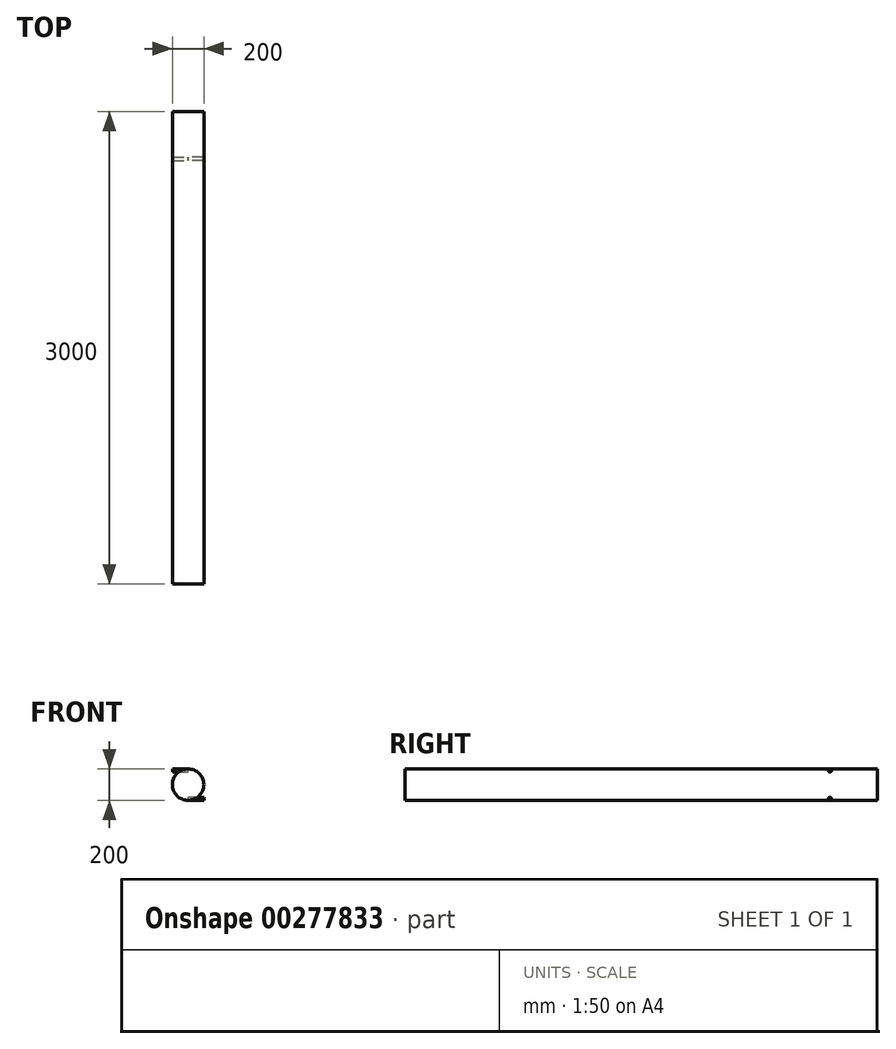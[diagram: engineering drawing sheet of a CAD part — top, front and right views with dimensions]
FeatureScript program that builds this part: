
annotation { "Feature Type Name" : "Feature", "Feature Type Description" : "" }
export const myFeature = defineFeature(function(context is Context, id is Id, definition is map)
    precondition{}
    {
        {
            var Q0;
            Q0=qCreatedBy(makeId("Front.planeOp"),FACE);
            var sketch = newSketch(context, id + "F0", { "sketchPlane" : qUnion([Q0])});
            skCircle(sketch, "E0", {"center": v(0, 0) * mm, "radius": 100 * mm});
            skSolve(sketch);
        }
        {
            var Q0;
            Q0=makeQuery(id+"F0.imprint","IMPRINT",FACE,{"disambiguationData":[TD([[makeQuery(id+"F0.imprint","IMPRINT",EDGE,{"derivedFrom":sQuery(id+"F0.wireOp",EDGE,"E0")}),1.0]])]});
            extrude(context, id + "F1", {"entities" : qUnion([Q0]), "depth" : 3000 * mm});
        }
        {
            var Q0;
            Q0=qCreatedBy(makeId("Right.planeOp"),FACE);
            var sketch = newSketch(context, id + "F2", { "sketchPlane" : qUnion([Q0])});
            skCircle(sketch, "E1", {"center": v(-300, 90) * mm, "radius": 10 * mm});
            skSolve(sketch);
        }
        {
            var Q0;
            Q0 = qSketchRegion(id + "F2", true);
            extrude(context, id + "F3", {"entities" : qUnion([Q0]), "oppositeDirection" : true, "depth" : 100 * mm});
        }
        {
            var Q0;
            Q0=makeQuery(id+"F3.opExtrude","SWEPT_BODY",BODY,{"disambiguationData":[OSD([sQuery(id+"F2.wireOp",EDGE,"E1")])]});
            var Q1;
            Q1=makeQuery(id+"F1.opExtrude","CAP_EDGE",EDGE,{"disambiguationData":[OSD([sQuery(id+"F0.wireOp",EDGE,"E0")])],"isStart":true});
            circularPattern(context, id + "F4", {"entities" : qUnion([Q0]), "axis" : qUnion([Q1]), "angle" : 360 * degree, "instanceCount" : 2, "oppositeDirection" : true, "equalSpace" : true});
        }
    });
